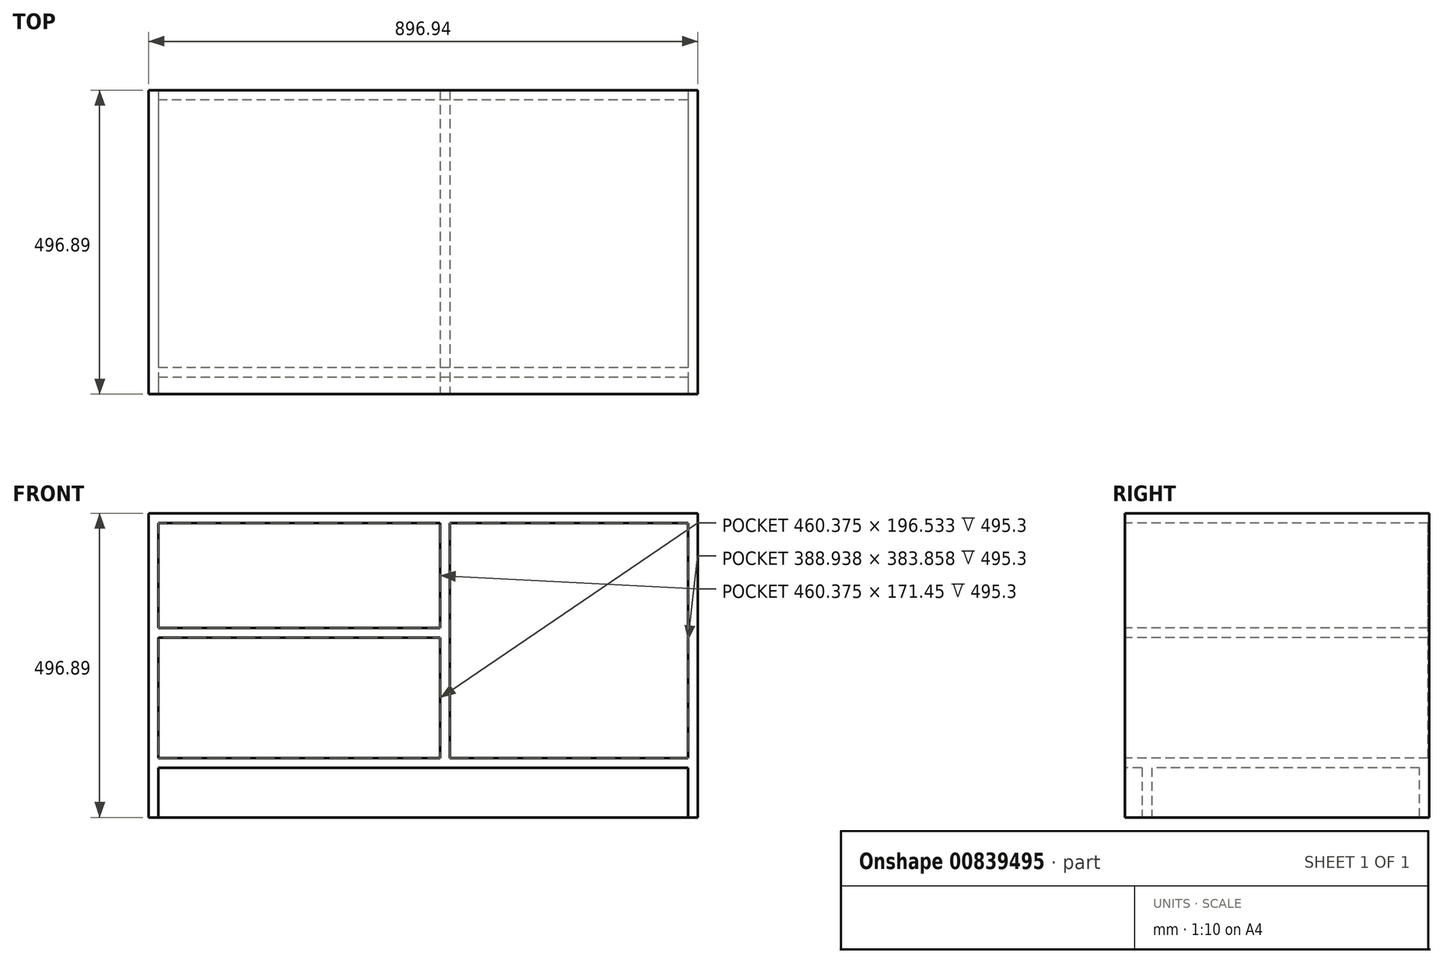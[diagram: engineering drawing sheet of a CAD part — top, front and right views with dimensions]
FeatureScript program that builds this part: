
annotation { "Feature Type Name" : "Feature", "Feature Type Description" : "" }
export const myFeature = defineFeature(function(context is Context, id is Id, definition is map)
    precondition{}
    {
        {
            var Q0;
            Q0=qCreatedBy(makeId("Front.planeOp"),FACE);
            var sketch = newSketch(context, id + "F0", { "sketchPlane" : qUnion([Q0])});
            skLineSegment(sketch, "E0.bottom", {"start": v(0, 0) * mm, "end": v(896.94, 0) * mm});
            skLineSegment(sketch, "E0.top", {"start": v(0, -496.89) * mm, "end": v(896.94, -496.89) * mm});
            skLineSegment(sketch, "E0.left", {"start": v(0, 0) * mm, "end": v(0, -496.89) * mm});
            skLineSegment(sketch, "E0.right", {"start": v(896.94, 0) * mm, "end": v(896.94, -496.89) * mm});
            skLineSegment(sketch, "E1.bottom", {"start": v(15.88, -15.88) * mm, "end": v(881.06, -15.88) * mm});
            skLineSegment(sketch, "E1.left", {"start": v(15.88, -15.87) * mm, "end": v(15.88, -496.89) * mm});
            skLineSegment(sketch, "E1.right", {"start": v(881.06, -15.87) * mm, "end": v(881.06, -496.89) * mm});
            skLineSegment(sketch, "E2", {"start": v(881.06, -15.88) * mm, "end": v(881.06, 0) * mm});
            skLineSegment(sketch, "E3", {"start": v(15.88, -15.88) * mm, "end": v(15.88, 0) * mm});
            skLineSegment(sketch, "E4", {"start": v(15.88, -415.6) * mm, "end": v(881.06, -415.6) * mm});
            skLineSegment(sketch, "E5", {"start": v(15.88, -399.73) * mm, "end": v(881.06, -399.73) * mm});
            skLineSegment(sketch, "E6", {"start": v(476.25, -15.87) * mm, "end": v(476.25, -399.73) * mm});
            skLineSegment(sketch, "E7", {"start": v(492.13, -15.87) * mm, "end": v(492.13, -399.73) * mm});
            skLineSegment(sketch, "E8", {"start": v(15.88, -187.33) * mm, "end": v(476.25, -187.32) * mm});
            skLineSegment(sketch, "E9", {"start": v(15.88, -203.2) * mm, "end": v(476.25, -203.2) * mm});
            skSolve(sketch);
        }
        {
            var Q0;
            {var subQ0=sQuery(id+"F0.wireOp",EDGE,"E2");Q0=makeQuery(id+"F0.imprint","IMPRINT",FACE,{"disambiguationData":[TD([[makeQuery(id+"F0.imprint","IMPRINT",EDGE,{"derivedFrom":subQ0}),1.0]])]});}
            var Q1;
            {var subQ3=sQuery(id+"F0.wireOp",EDGE,"E0.right");Q1=makeQuery(id+"F0.imprint","IMPRINT",FACE,{"disambiguationData":[TD([[makeQuery(id+"F0.imprint","IMPRINT",EDGE,{"derivedFrom":subQ3}),-1.0]])]});}
            var Q2;
            {var subQ3=sQuery(id+"F0.wireOp",EDGE,"E0.left");Q2=makeQuery(id+"F0.imprint","IMPRINT",FACE,{"disambiguationData":[TD([[makeQuery(id+"F0.imprint","IMPRINT",EDGE,{"derivedFrom":subQ3}),1.0]])]});}
            var Q3;
            {var subQ0=sQuery(id+"F0.wireOp",EDGE,"E8");Q3=makeQuery(id+"F0.imprint","IMPRINT",FACE,{"disambiguationData":[TD([[makeQuery(id+"F0.imprint","IMPRINT",EDGE,{"derivedFrom":subQ0}),-1.0]])]});}
            var Q4;
            {var subQ7=sQuery(id+"F0.wireOp",EDGE,"E7");Q4=makeQuery(id+"F0.imprint","IMPRINT",FACE,{"disambiguationData":[TD([[makeQuery(id+"F0.imprint","IMPRINT",EDGE,{"derivedFrom":subQ7}),-1.0]])]});}
            var Q5;
            {var subQ0=sQuery(id+"F0.wireOp",EDGE,"E4");Q5=makeQuery(id+"F0.imprint","IMPRINT",FACE,{"disambiguationData":[TD([[makeQuery(id+"F0.imprint","IMPRINT",EDGE,{"derivedFrom":subQ0}),1.0]])]});}
            extrude(context, id + "F1", {"entities" : qUnion([Q0, Q1, Q2, Q3, Q4, Q5]), "oppositeDirection" : true, "depth" : 496.9 * mm, "offsetDistance" : 25.4 * mm});
        }
        {
            var Q0;
            {var subQ5=sQuery(id+"F0.wireOp",EDGE,"E4");Q0=makeQuery(id+"F0.imprint","IMPRINT",FACE,{"disambiguationData":[TD([[makeQuery(id+"F0.imprint","IMPRINT",EDGE,{"derivedFrom":subQ5}),-1.0]])]});}
            extrude(context, id + "F2", {"entities" : qUnion([Q0]), "operationType" : NewBodyOperationType.ADD, "oppositeDirection" : true, "depth" : 43.81 * mm, "offsetDistance" : 25.4 * mm, "hasSecondDirection" : true, "secondDirectionOppositeDirection" : true, "secondDirectionDepth" : 27.94 * mm});
        }
        {
            var Q0;
            Q0=makeQuery(id+"F2.opExtrude","CAP_FACE",FACE,{"disambiguationData":[OSD([sQuery(id+"F0.wireOp",EDGE,"E0.top"),sQuery(id+"F0.wireOp",EDGE,"E1.left"),sQuery(id+"F0.wireOp",EDGE,"E1.right"),sQuery(id+"F0.wireOp",EDGE,"E4")])],"isStart":false});
            var Q1;
            Q1=makeQuery(id+"F1.opExtrude","CAP_FACE",FACE,{"disambiguationData":[OSD([sQuery(id+"F0.wireOp",EDGE,"E0.bottom"),sQuery(id+"F0.wireOp",EDGE,"E0.top"),sQuery(id+"F0.wireOp",EDGE,"E0.left"),sQuery(id+"F0.wireOp",EDGE,"E0.right"),sQuery(id+"F0.wireOp",EDGE,"E1.bottom"),sQuery(id+"F0.wireOp",EDGE,"E1.left"),sQuery(id+"F0.wireOp",EDGE,"E1.right"),sQuery(id+"F0.wireOp",EDGE,"E4"),sQuery(id+"F0.wireOp",EDGE,"E5"),sQuery(id+"F0.wireOp",EDGE,"E6"),sQuery(id+"F0.wireOp",EDGE,"E7"),sQuery(id+"F0.wireOp",EDGE,"E8"),sQuery(id+"F0.wireOp",EDGE,"E9")])],"isStart":false});
            var Q2;
            Q2=makeQuery(id+"F1.opExtrude","CAP_FACE",FACE,{"disambiguationData":[OSD([sQuery(id+"F0.wireOp",EDGE,"E0.bottom"),sQuery(id+"F0.wireOp",EDGE,"E0.top"),sQuery(id+"F0.wireOp",EDGE,"E0.left"),sQuery(id+"F0.wireOp",EDGE,"E0.right"),sQuery(id+"F0.wireOp",EDGE,"E1.bottom"),sQuery(id+"F0.wireOp",EDGE,"E1.left"),sQuery(id+"F0.wireOp",EDGE,"E1.right"),sQuery(id+"F0.wireOp",EDGE,"E4"),sQuery(id+"F0.wireOp",EDGE,"E5"),sQuery(id+"F0.wireOp",EDGE,"E6"),sQuery(id+"F0.wireOp",EDGE,"E7"),sQuery(id+"F0.wireOp",EDGE,"E8"),sQuery(id+"F0.wireOp",EDGE,"E9")])],"isStart":false});
            extrude(context, id + "F3", {"entities" : qUnion([Q0]), "operationType" : NewBodyOperationType.ADD, "endBound" : BoundingType.UP_TO_SURFACE, "depth" : 317.5 * mm, "endBoundEntityFace" : qUnion([Q1]), "offsetDistance" : 25.4 * mm, "hasSecondDirection" : true, "secondDirectionBound" : BoundingType.UP_TO_SURFACE, "secondDirectionOppositeDirection" : false, "secondDirectionDepth" : 287.02 * mm, "secondDirectionBoundEntityFace" : qUnion([Q2]), "hasSecondDirectionOffset" : true, "secondDirectionOffsetDistance" : 15.88 * mm});
        }
        {
            var Q0;
            {var subQ5=sQuery(id+"F0.wireOp",EDGE,"E4");Q0=makeQuery(id+"F0.imprint","IMPRINT",FACE,{"disambiguationData":[TD([[makeQuery(id+"F0.imprint","IMPRINT",EDGE,{"derivedFrom":subQ5}),-1.0]])]});}
            var Q1;
            {var subQ0=sQuery(id+"F0.wireOp",EDGE,"E4");Q1=makeQuery(id+"F0.imprint","IMPRINT",FACE,{"disambiguationData":[TD([[makeQuery(id+"F0.imprint","IMPRINT",EDGE,{"derivedFrom":subQ0}),1.0]])]});}
            var Q2;
            {var subQ3=sQuery(id+"F0.wireOp",EDGE,"E9");Q2=makeQuery(id+"F0.imprint","IMPRINT",FACE,{"disambiguationData":[TD([[makeQuery(id+"F0.imprint","IMPRINT",EDGE,{"derivedFrom":subQ3}),-1.0]])]});}
            var Q3;
            {var subQ3=sQuery(id+"F0.wireOp",EDGE,"E7");Q3=makeQuery(id+"F0.imprint","IMPRINT",FACE,{"disambiguationData":[TD([[makeQuery(id+"F0.imprint","IMPRINT",EDGE,{"derivedFrom":subQ3}),1.0]])]});}
            var Q4;
            {var subQ0=sQuery(id+"F0.wireOp",EDGE,"E8");Q4=makeQuery(id+"F0.imprint","IMPRINT",FACE,{"disambiguationData":[TD([[makeQuery(id+"F0.imprint","IMPRINT",EDGE,{"derivedFrom":subQ0}),-1.0]])]});}
            var Q5;
            {var subQ7=sQuery(id+"F0.wireOp",EDGE,"E7");Q5=makeQuery(id+"F0.imprint","IMPRINT",FACE,{"disambiguationData":[TD([[makeQuery(id+"F0.imprint","IMPRINT",EDGE,{"derivedFrom":subQ7}),-1.0]])]});}
            var Q6;
            {var subQ5=sQuery(id+"F0.wireOp",EDGE,"E8");Q6=makeQuery(id+"F0.imprint","IMPRINT",FACE,{"disambiguationData":[TD([[makeQuery(id+"F0.imprint","IMPRINT",EDGE,{"derivedFrom":subQ5}),1.0]])]});}
            var Q7;
            {var subQ0=sQuery(id+"F0.wireOp",EDGE,"E2");Q7=makeQuery(id+"F0.imprint","IMPRINT",FACE,{"disambiguationData":[TD([[makeQuery(id+"F0.imprint","IMPRINT",EDGE,{"derivedFrom":subQ0}),1.0]])]});}
            var Q8;
            {var subQ3=sQuery(id+"F0.wireOp",EDGE,"E0.right");Q8=makeQuery(id+"F0.imprint","IMPRINT",FACE,{"disambiguationData":[TD([[makeQuery(id+"F0.imprint","IMPRINT",EDGE,{"derivedFrom":subQ3}),-1.0]])]});}
            var Q9;
            {var subQ3=sQuery(id+"F0.wireOp",EDGE,"E0.left");Q9=makeQuery(id+"F0.imprint","IMPRINT",FACE,{"disambiguationData":[TD([[makeQuery(id+"F0.imprint","IMPRINT",EDGE,{"derivedFrom":subQ3}),1.0]])]});}
            var Q10;
            {var subQ0=sQuery(id+"F0.wireOp",EDGE,"E9");var subQ1=sQuery(id+"F0.wireOp",EDGE,"E8");var subQ2=sQuery(id+"F0.wireOp",EDGE,"E7");var subQ3=sQuery(id+"F0.wireOp",EDGE,"E6");var subQ4=sQuery(id+"F0.wireOp",EDGE,"E5");var subQ5=sQuery(id+"F0.wireOp",EDGE,"E4");var subQ6=sQuery(id+"F0.wireOp",EDGE,"E1.right");var subQ7=sQuery(id+"F0.wireOp",EDGE,"E1.left");var subQ8=sQuery(id+"F0.wireOp",EDGE,"E1.bottom");var subQ9=sQuery(id+"F0.wireOp",EDGE,"E0.right");var subQ10=sQuery(id+"F0.wireOp",EDGE,"E0.left");var subQ11=sQuery(id+"F0.wireOp",EDGE,"E0.top");var subQ12=sQuery(id+"F0.wireOp",EDGE,"E0.bottom");Q10=makeQuery(id+"F3.boolean.opBoolean","MERGE",FACE,{"derivedFrom":[makeQuery(id+"F1.opExtrude","CAP_FACE",FACE,{"disambiguationData":[OSD([subQ12,subQ11,subQ10,subQ9,subQ8,subQ7,subQ6,subQ5,subQ4,subQ3,subQ2,subQ1,subQ0])],"isStart":false}),makeQuery(id+"F3.opExtrude","CAP_FACE",FACE,{"disambiguationData":[OSD([subQ12,subQ11,subQ10,subQ9,subQ8,subQ7,subQ6,subQ5,subQ4,subQ3,subQ2,subQ1,subQ0])],"isStart":false})]});}
            extrude(context, id + "F4", {"entities" : qUnion([Q0, Q1, Q2, Q3, Q4, Q5, Q6, Q7, Q8, Q9]), "operationType" : NewBodyOperationType.ADD, "endBound" : BoundingType.UP_TO_SURFACE, "oppositeDirection" : true, "depth" : 320.04 * mm, "endBoundEntityFace" : qUnion([Q10]), "offsetDistance" : 25.4 * mm, "hasSecondDirection" : true, "secondDirectionOppositeDirection" : true, "secondDirectionDepth" : 495.3 * mm});
        }
    });
